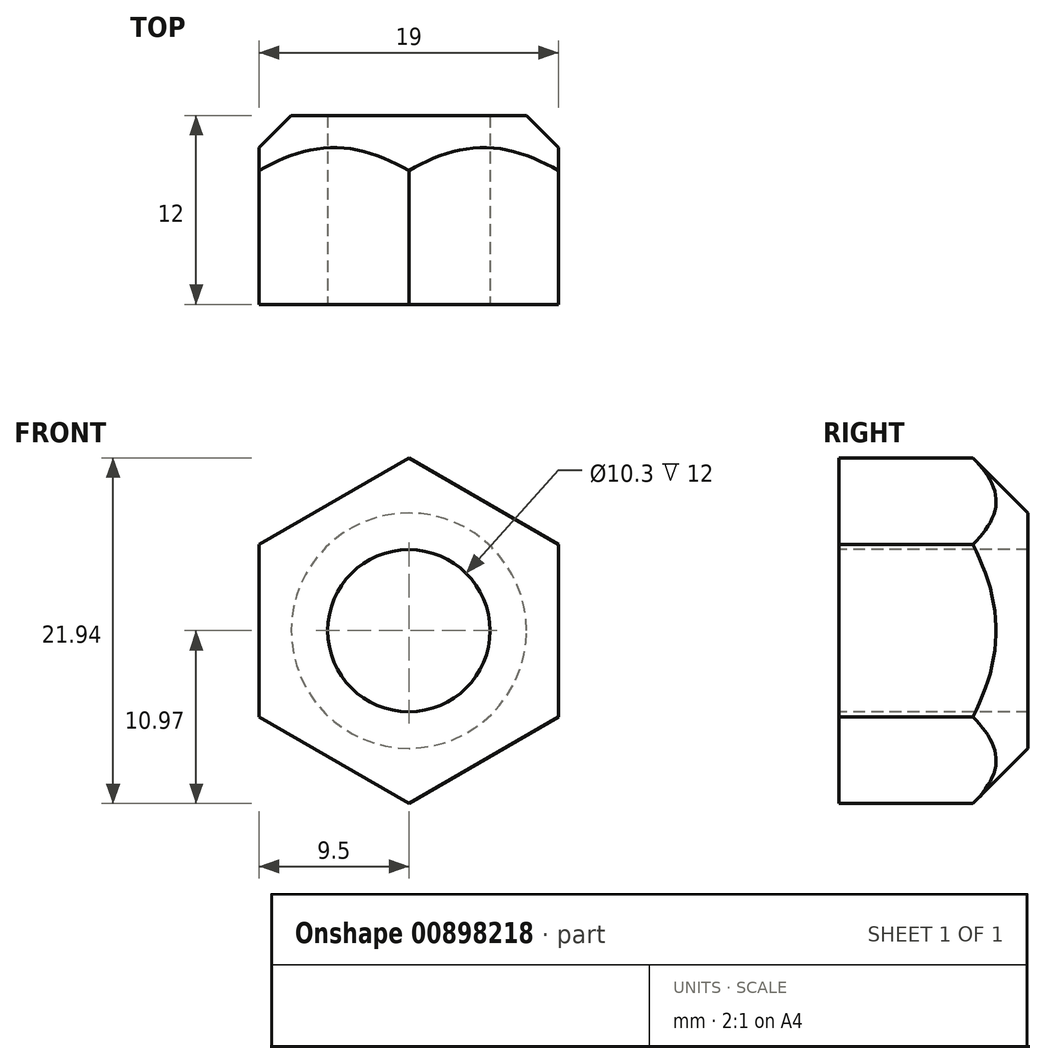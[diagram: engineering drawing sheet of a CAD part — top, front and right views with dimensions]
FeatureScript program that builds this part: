
annotation { "Feature Type Name" : "Feature", "Feature Type Description" : "" }
export const myFeature = defineFeature(function(context is Context, id is Id, definition is map)
    precondition{}
    {
        {
            var Q0;
            Q0=qCreatedBy(makeId("Front.planeOp"),FACE);
            var sketch = newSketch(context, id + "F0", { "sketchPlane" : qUnion([Q0])});
            skCircle(sketch, "E0.cCircle", {"center": v(0, 0) * mm, "radius": 9.5 * mm});
            skLineSegment(sketch, "E0.0", {"start": v(9.5, 5.48) * mm, "end": v(9.5, -5.48) * mm});
            skLineSegment(sketch, "E0.1", {"start": v(9.5, -5.48) * mm, "end": v(0, -10.97) * mm});
            skLineSegment(sketch, "E0.2", {"start": v(0, -10.97) * mm, "end": v(-9.5, -5.48) * mm});
            skLineSegment(sketch, "E0.3", {"start": v(-9.5, -5.48) * mm, "end": v(-9.5, 5.48) * mm});
            skLineSegment(sketch, "E0.4", {"start": v(-9.5, 5.48) * mm, "end": v(0, 10.97) * mm});
            skLineSegment(sketch, "E0.5", {"start": v(0, 10.97) * mm, "end": v(9.5, 5.48) * mm});
            skPoint(sketch, "E0.0.midPoint", {"position": v(9.5, 0) * mm});
            skCircle(sketch, "E1", {"center": v(0, 0) * mm, "radius": 10.97 * mm});
            skSolve(sketch);
        }
        {
            var Q0;
            Q0=qCreatedBy(makeId("Right.planeOp"),FACE);
            var sketch = newSketch(context, id + "F1", { "sketchPlane" : qUnion([Q0])});
            skPoint(sketch, "E2.0", {"position": v(0, 10.97) * mm});
            skLineSegment(sketch, "E2.1", {"start": v(0, -9.5) * mm, "end": v(0, 9.5) * mm});
            skLineSegment(sketch, "E3", {"start": v(0, 10.97) * mm, "end": v(8.5, 10.97) * mm});
            skLineSegment(sketch, "E4", {"start": v(0, 0) * mm, "end": v(12, 0) * mm});
            skLineSegment(sketch, "E5", {"start": v(12, 0) * mm, "end": v(12, 7.47) * mm});
            skLineSegment(sketch, "E6", {"start": v(12, 7.47) * mm, "end": v(8.5, 10.97) * mm});
            skLineSegment(sketch, "E7", {"start": v(0, 10.97) * mm, "end": v(0, 0) * mm});
            skSolve(sketch);
        }
        {
            var Q0;
            {var subQ1=sQuery(id+"F1.wireOp",EDGE,"E3");Q0=makeQuery(id+"F1.imprint","IMPRINT",FACE,{"disambiguationData":[TD([[makeQuery(id+"F1.imprint","IMPRINT",EDGE,{"derivedFrom":subQ1}),-1.0]])]});}
            var Q1;
            Q1=sQuery(id+"F1.wireOp",EDGE,"E4");
            revolve(context, id + "F2", {"surfaceOperationType" : NewSurfaceOperationType.NEW, "entities" : qUnion([Q0]), "axis" : qUnion([Q1]), "revolveType" : RevolveType.FULL});
        }
        {
            var Q0;
            {var subQ1=sQuery(id+"F0.wireOp",EDGE,"E0.3");var subQ3=makeQuery(id+"F0.imprint","INTERSECT",VERTEX,{"derivedFrom":[sQuery(id+"F0.wireOp",EDGE,"E0.cCircle"),subQ1]});Q0=makeQuery(id+"F0.imprint","IMPRINT",FACE,{"disambiguationData":[TD([[makeQuery(id+"F0.imprint","IMPRINT",EDGE,{"disambiguationData":[TD([[subQ3,1.0]])],"derivedFrom":subQ1}),1.0]])]});}
            var Q1;
            {var subQ1=sQuery(id+"F0.wireOp",EDGE,"E0.4");var subQ3=makeQuery(id+"F0.imprint","INTERSECT",VERTEX,{"derivedFrom":[sQuery(id+"F0.wireOp",EDGE,"E0.cCircle"),subQ1]});Q1=makeQuery(id+"F0.imprint","IMPRINT",FACE,{"disambiguationData":[TD([[makeQuery(id+"F0.imprint","IMPRINT",EDGE,{"disambiguationData":[TD([[subQ3,1.0]])],"derivedFrom":subQ1}),1.0]])]});}
            var Q2;
            {var subQ1=sQuery(id+"F0.wireOp",EDGE,"E0.5");var subQ3=makeQuery(id+"F0.imprint","INTERSECT",VERTEX,{"derivedFrom":[sQuery(id+"F0.wireOp",EDGE,"E0.cCircle"),subQ1]});Q2=makeQuery(id+"F0.imprint","IMPRINT",FACE,{"disambiguationData":[TD([[makeQuery(id+"F0.imprint","IMPRINT",EDGE,{"disambiguationData":[TD([[subQ3,1.0]])],"derivedFrom":subQ1}),1.0]])]});}
            var Q3;
            {var subQ1=sQuery(id+"F0.wireOp",EDGE,"E0.0");var subQ3=makeQuery(id+"F0.imprint","INTERSECT",VERTEX,{"derivedFrom":[sQuery(id+"F0.wireOp",EDGE,"E0.cCircle"),subQ1]});Q3=makeQuery(id+"F0.imprint","IMPRINT",FACE,{"disambiguationData":[TD([[makeQuery(id+"F0.imprint","IMPRINT",EDGE,{"disambiguationData":[TD([[subQ3,1.0]])],"derivedFrom":subQ1}),1.0]])]});}
            var Q4;
            {var subQ1=sQuery(id+"F0.wireOp",EDGE,"E0.1");var subQ3=makeQuery(id+"F0.imprint","INTERSECT",VERTEX,{"derivedFrom":[sQuery(id+"F0.wireOp",EDGE,"E0.cCircle"),subQ1]});Q4=makeQuery(id+"F0.imprint","IMPRINT",FACE,{"disambiguationData":[TD([[makeQuery(id+"F0.imprint","IMPRINT",EDGE,{"disambiguationData":[TD([[subQ3,1.0]])],"derivedFrom":subQ1}),1.0]])]});}
            var Q5;
            {var subQ1=sQuery(id+"F0.wireOp",EDGE,"E0.2");var subQ3=makeQuery(id+"F0.imprint","INTERSECT",VERTEX,{"derivedFrom":[sQuery(id+"F0.wireOp",EDGE,"E0.cCircle"),subQ1]});Q5=makeQuery(id+"F0.imprint","IMPRINT",FACE,{"disambiguationData":[TD([[makeQuery(id+"F0.imprint","IMPRINT",EDGE,{"disambiguationData":[TD([[subQ3,1.0]])],"derivedFrom":subQ1}),1.0]])]});}
            extrude(context, id + "F3", {"entities" : qUnion([Q0, Q1, Q2, Q3, Q4, Q5]), "operationType" : NewBodyOperationType.REMOVE, "endBound" : BoundingType.THROUGH_ALL, "oppositeDirection" : true, "depth" : 25 * mm, "offsetDistance" : 25 * mm});
        }
        {
            var Q0;
            Q0=sQuery(id+"F0.wireOp",VERTEX,"E0.cCircle.center");
            var Q1;
            Q1=makeQuery(id+"F2.opRevolve","SWEPT_BODY",BODY,{"disambiguationData":[OSD([sQuery(id+"F1.wireOp",EDGE,"E3"),sQuery(id+"F1.wireOp",EDGE,"E4"),sQuery(id+"F1.wireOp",EDGE,"E5"),sQuery(id+"F1.wireOp",EDGE,"E6"),sQuery(id+"F1.wireOp",EDGE,"E7")])]});
            hole(context, id + "F4", {"style" : HoleStyle.SIMPLE, "endStyle" : HoleEndStyle.THROUGH, "standardTappedOrClearance" : lookupTablePath({ "standard" : "ISO", "engagement" : "75%", "pitch" : "1.75 mm", "size" : "M12", "type" : "Tapped" }), "standardBlindInLast" : lookupTablePath({ "standard" : "ISO", "engagement" : "75%", "pitch" : "1.75 mm", "size" : "M12", "type" : "Tapped" }), "holeDiameter" : 10.3 * mm, "majorDiameter" : 12 * mm, "showTappedDepth" : true, "isTappedThrough" : true, "tappedDepth" : 14 * mm, "tapClearance" : 3, "locations" : qUnion([Q0]), "scope" : qUnion([Q1])});
        }
    });
